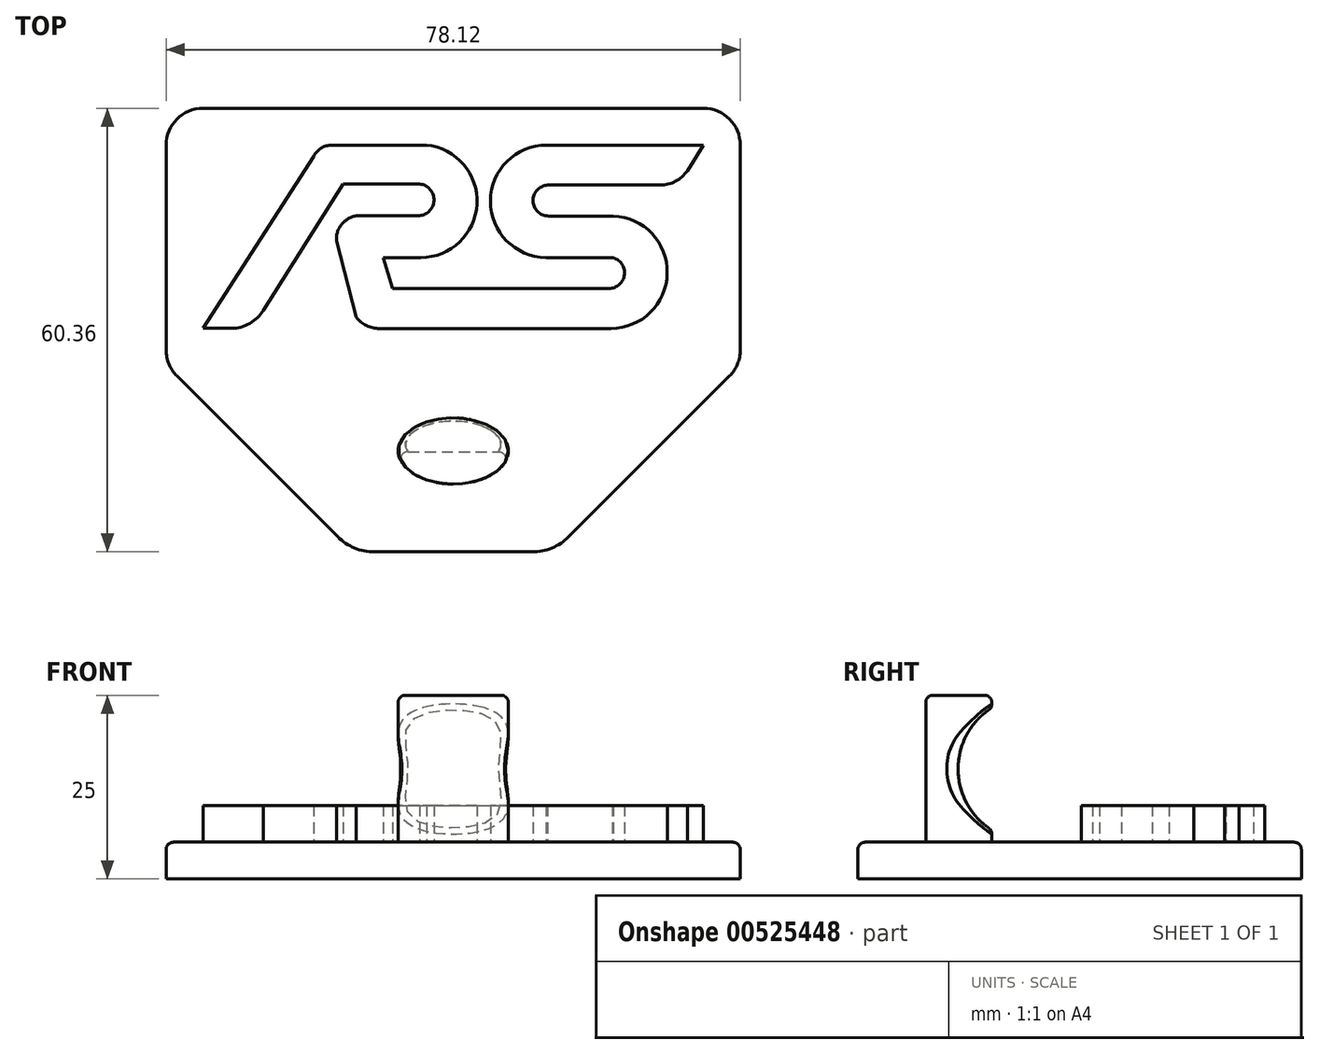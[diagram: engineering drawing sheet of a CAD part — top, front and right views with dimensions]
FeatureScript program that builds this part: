
annotation { "Feature Type Name" : "Feature", "Feature Type Description" : "" }
export const myFeature = defineFeature(function(context is Context, id is Id, definition is map)
    precondition{}
    {
        {
            var Q0;
            Q0=qCreatedBy(makeId("Top.planeOp"),FACE);
            var sketch = newSketch(context, id + "F0", { "sketchPlane" : qUnion([Q0])});
            skLineSegment(sketch, "E0", {"start": v(-38.04, -12.57) * mm, "end": v(-22.97, 10.83) * mm});
            skLineSegment(sketch, "E1", {"start": v(8.97, 2.72) * mm, "end": v(17.8, 2.72) * mm});
            skLineSegment(sketch, "E2", {"start": v(-12.22, -7.15) * mm, "end": v(17.2, -7.15) * mm});
            skLineSegment(sketch, "E3", {"start": v(8.73, 12.37) * mm, "end": v(30.08, 12.37) * mm});
            skLineSegment(sketch, "E4", {"start": v(-18.96, 7.08) * mm, "end": v(-8.76, 7.08) * mm});
            skLineSegment(sketch, "E5", {"start": v(-13.5, -2.94) * mm, "end": v(-8.4, -2.94) * mm});
            skLineSegment(sketch, "E6", {"start": v(8.63, -2.94) * mm, "end": v(17.65, -2.94) * mm});
            skLineSegment(sketch, "E7", {"start": v(-18.96, 7.08) * mm, "end": v(-29.82, -10.1) * mm});
            skLineSegment(sketch, "E8", {"start": v(-38.04, -12.57) * mm, "end": v(-34.18, -12.57) * mm});
            skLineSegment(sketch, "E9", {"start": v(-14.02, -12.59) * mm, "end": v(17.48, -12.59) * mm});
            skLineSegment(sketch, "E10", {"start": v(-8.57, 2.77) * mm, "end": v(-16.7, 2.77) * mm});
            skLineSegment(sketch, "E11", {"start": v(-19.87, -0.65) * mm, "end": v(-17.2, -11.05) * mm});
            skArc(sketch, "E12", {"start": v(-34.18, -12.57) * mm, "mid": v(-31.68, -11.91) * mm, "end": v(-29.82, -10.1) * mm});
            skLineSegment(sketch, "E13", {"start": v(-20.5, 12.37) * mm, "end": v(-7.63, 12.37) * mm});
            skArc(sketch, "E14", {"start": v(-20.5, 12.37) * mm, "mid": v(-21.95, 11.95) * mm, "end": v(-22.97, 10.83) * mm});
            skArc(sketch, "E15", {"start": v(-8.57, 2.77) * mm, "mid": v(-6.6, 5.01) * mm, "end": v(-8.76, 7.08) * mm});
            skArc(sketch, "E16", {"start": v(-16.7, 2.77) * mm, "mid": v(-19.03, 1.75) * mm, "end": v(-19.87, -0.65) * mm});
            skArc(sketch, "E17", {"start": v(-8.4, -2.94) * mm, "mid": v(-0.74, 4.34) * mm, "end": v(-7.63, 12.37) * mm});
            skArc(sketch, "E18", {"start": v(8.73, 12.37) * mm, "mid": v(1.08, 4.76) * mm, "end": v(8.63, -2.94) * mm});
            skArc(sketch, "E19", {"start": v(17.48, -12.59) * mm, "mid": v(25.13, -5.08) * mm, "end": v(17.8, 2.72) * mm});
            skArc(sketch, "E20", {"start": v(17.2, -7.15) * mm, "mid": v(19.32, -5.24) * mm, "end": v(17.65, -2.94) * mm});
            skArc(sketch, "E21", {"start": v(-17.2, -11.05) * mm, "mid": v(-15.78, -12.18) * mm, "end": v(-14.02, -12.59) * mm});
            skLineSegment(sketch, "E22", {"start": v(30.08, 12.37) * mm, "end": v(27.89, 8.87) * mm});
            skLineSegment(sketch, "E23", {"start": v(8.87, 6.92) * mm, "end": v(24.17, 6.92) * mm});
            skArc(sketch, "E24", {"start": v(8.87, 6.92) * mm, "mid": v(6.88, 4.77) * mm, "end": v(8.97, 2.72) * mm});
            skArc(sketch, "E25", {"start": v(24.17, 6.92) * mm, "mid": v(26.27, 7.44) * mm, "end": v(27.89, 8.87) * mm});
            skLineSegment(sketch, "E26", {"start": v(-13.5, -2.94) * mm, "end": v(-12.22, -7.15) * mm});
            skSolve(sketch);
        }
        {
            var Q0;
            Q0 = qSketchRegion(id + "F0", true);
            extrude(context, id + "F1", {"entities" : qUnion([Q0]), "depth" : 5 * mm, "offsetDistance" : 25 * mm});
        }
        {
            var Q0;
            Q0=makeQuery(id+"F1.opExtrude","CAP_FACE",FACE,{"disambiguationData":[OSD([sQuery(id+"F0.wireOp",EDGE,"E0"),sQuery(id+"F0.wireOp",EDGE,"E1"),sQuery(id+"F0.wireOp",EDGE,"E2"),sQuery(id+"F0.wireOp",EDGE,"E3"),sQuery(id+"F0.wireOp",EDGE,"E4"),sQuery(id+"F0.wireOp",EDGE,"E5"),sQuery(id+"F0.wireOp",EDGE,"E6"),sQuery(id+"F0.wireOp",EDGE,"E7"),sQuery(id+"F0.wireOp",EDGE,"E8"),sQuery(id+"F0.wireOp",EDGE,"E9"),sQuery(id+"F0.wireOp",EDGE,"E10"),sQuery(id+"F0.wireOp",EDGE,"E11"),sQuery(id+"F0.wireOp",EDGE,"E12"),sQuery(id+"F0.wireOp",EDGE,"E13"),sQuery(id+"F0.wireOp",EDGE,"E14"),sQuery(id+"F0.wireOp",EDGE,"E15"),sQuery(id+"F0.wireOp",EDGE,"E16"),sQuery(id+"F0.wireOp",EDGE,"E17"),sQuery(id+"F0.wireOp",EDGE,"E18"),sQuery(id+"F0.wireOp",EDGE,"E19"),sQuery(id+"F0.wireOp",EDGE,"E20"),sQuery(id+"F0.wireOp",EDGE,"E21"),sQuery(id+"F0.wireOp",EDGE,"E22"),sQuery(id+"F0.wireOp",EDGE,"E23"),sQuery(id+"F0.wireOp",EDGE,"E24"),sQuery(id+"F0.wireOp",EDGE,"E25"),sQuery(id+"F0.wireOp",EDGE,"E26")])],"isStart":true});
            var sketch = newSketch(context, id + "F2", { "sketchPlane" : qUnion([Q0])});
            skLineSegment(sketch, "E27.bottom", {"start": v(-38.04, -17.37) * mm, "end": v(30.08, -17.37) * mm});
            skLineSegment(sketch, "E27.top", {"start": v(-43.04, 17.59) * mm, "end": v(35.08, 17.59) * mm});
            skLineSegment(sketch, "E27.left", {"start": v(-43.04, -12.37) * mm, "end": v(-43.04, 17.59) * mm});
            skLineSegment(sketch, "E27.right", {"start": v(35.08, -12.37) * mm, "end": v(35.08, 17.59) * mm});
            skPoint(sketch, "E28.visualSharp", {"position": v(-43.04, -17.37) * mm});
            skArc(sketch, "E28.filletArc", {"start": v(-43.04, -12.37) * mm, "mid": v(-41.58, -15.9) * mm, "end": v(-38.04, -17.37) * mm});
            skPoint(sketch, "E29.visualSharp", {"position": v(35.08, -17.37) * mm});
            skArc(sketch, "E29.filletArc", {"start": v(30.08, -17.37) * mm, "mid": v(33.62, -15.9) * mm, "end": v(35.08, -12.37) * mm});
            skPoint(sketch, "E30.visualSharp", {"position": v(-43.04, 17.59) * mm});
            skSolve(sketch);
        }
        {
            var Q0;
            Q0 = qSketchRegion(id + "F2", true);
            extrude(context, id + "F3", {"entities" : qUnion([Q0]), "operationType" : NewBodyOperationType.ADD, "depth" : 5 * mm, "offsetDistance" : 25 * mm});
        }
        {
            var Q0;
            Q0=makeQuery(id+"F3.opExtrude","CAP_FACE",FACE,{"disambiguationData":[OSD([sQuery(id+"F2.wireOp",EDGE,"E27.bottom"),sQuery(id+"F2.wireOp",EDGE,"E27.top"),sQuery(id+"F2.wireOp",EDGE,"E27.left"),sQuery(id+"F2.wireOp",EDGE,"E27.right"),sQuery(id+"F2.wireOp",EDGE,"E28.filletArc"),sQuery(id+"F2.wireOp",EDGE,"E29.filletArc"),sQuery(id+"F2.wireOp",EDGE,"744ff583-1bf7-4c06-8853-35fc34389462.filletArc"),sQuery(id+"F2.wireOp",EDGE,"E30.filletArc")])],"isStart":true});
            var sketch = newSketch(context, id + "F4", { "sketchPlane" : qUnion([Q0])});
            skLineSegment(sketch, "E31", {"start": v(-43.04, -17.59) * mm, "end": v(-19.7, -40.94) * mm});
            skLineSegment(sketch, "E32", {"start": v(35.08, -17.59) * mm, "end": v(11.73, -40.94) * mm});
            skLineSegment(sketch, "E33", {"start": v(-14.74, -42.99) * mm, "end": v(6.78, -42.99) * mm});
            skPoint(sketch, "E34.visualSharp", {"position": v(-17.64, -42.99) * mm});
            skArc(sketch, "E34.filletArc", {"start": v(-19.7, -40.94) * mm, "mid": v(-17.42, -42.45) * mm, "end": v(-14.74, -42.99) * mm});
            skPoint(sketch, "E35.visualSharp", {"position": v(9.68, -42.99) * mm});
            skArc(sketch, "E35.filletArc", {"start": v(6.78, -42.99) * mm, "mid": v(9.46, -42.45) * mm, "end": v(11.73, -40.94) * mm});
            skLineSegment(sketch, "E36", {"start": v(-43.04, -17.59) * mm, "end": v(35.08, -17.59) * mm});
            skSolve(sketch);
        }
        {
            var Q0;
            Q0 = qSketchRegion(id + "F4", true);
            extrude(context, id + "F5", {"entities" : qUnion([Q0]), "operationType" : NewBodyOperationType.ADD, "oppositeDirection" : true, "depth" : 5 * mm, "offsetDistance" : 25 * mm});
        }
        {
            var Q0;
            {var subQ0=sQuery(id+"F2.wireOp",EDGE,"E27.left");Q0=makeQuery(id+"F5.boolean.opBoolean","MERGE",EDGE,{"derivedFrom":[makeQuery(id+"F3.opExtrude","SWEPT_EDGE",EDGE,{"disambiguationData":[OSD([sQuery(id+"F2.wireOp",EDGE,"E27.top"),subQ0])]}),makeQuery(id+"F5.opExtrude","SWEPT_EDGE",EDGE,{"disambiguationData":[OSD([subQ0,sQuery(id+"F4.wireOp",EDGE,"E31"),sQuery(id+"F4.wireOp",EDGE,"E36")])]})]});}
            var Q1;
            {var subQ0=sQuery(id+"F2.wireOp",EDGE,"E27.right");Q1=makeQuery(id+"F5.boolean.opBoolean","MERGE",EDGE,{"derivedFrom":[makeQuery(id+"F3.opExtrude","SWEPT_EDGE",EDGE,{"disambiguationData":[OSD([sQuery(id+"F2.wireOp",EDGE,"E27.top"),subQ0])]}),makeQuery(id+"F5.opExtrude","SWEPT_EDGE",EDGE,{"disambiguationData":[OSD([subQ0,sQuery(id+"F4.wireOp",EDGE,"E32"),sQuery(id+"F4.wireOp",EDGE,"E36")])]})]});}
            fillet(context, id + "F6", {"entities" : qUnion([Q0, Q1]), "radius" : 5 * mm, "tangentPropagation" : true, "allowEdgeOverflow" : false});
        }
        {
            var Q0;
            Q0=makeQuery(id+"F5.boolean.opBoolean","MERGE",FACE,{"derivedFrom":[makeQuery(id+"F3.opExtrude","CAP_FACE",FACE,{"disambiguationData":[OSD([sQuery(id+"F2.wireOp",EDGE,"E27.bottom"),sQuery(id+"F2.wireOp",EDGE,"E27.top"),sQuery(id+"F2.wireOp",EDGE,"E27.left"),sQuery(id+"F2.wireOp",EDGE,"E27.right"),sQuery(id+"F2.wireOp",EDGE,"E28.filletArc"),sQuery(id+"F2.wireOp",EDGE,"E29.filletArc")])],"isStart":true}),makeQuery(id+"F5.opExtrude","CAP_FACE",FACE,{"disambiguationData":[OSD([sQuery(id+"F4.wireOp",EDGE,"E31"),sQuery(id+"F4.wireOp",EDGE,"E32"),sQuery(id+"F4.wireOp",EDGE,"E33"),sQuery(id+"F4.wireOp",EDGE,"E34.filletArc"),sQuery(id+"F4.wireOp",EDGE,"E35.filletArc"),sQuery(id+"F4.wireOp",EDGE,"E36")])],"isStart":true})]});
            var sketch = newSketch(context, id + "F7", { "sketchPlane" : qUnion([Q0])});
            skEllipse(sketch, "E37", {"center": v(-3.98, -29.25) * mm, "majorRadius": 7.5 * mm, "minorRadius": 4.5 * mm, "majorAxis": v(1, 0)});
            skSolve(sketch);
        }
        {
            var Q0;
            Q0 = qSketchRegion(id + "F7", true);
            extrude(context, id + "F8", {"entities" : qUnion([Q0]), "operationType" : NewBodyOperationType.ADD, "depth" : 20 * mm, "offsetDistance" : 25 * mm});
        }
        {
            var Q0;
            Q0=qCreatedBy(makeId("Right.planeOp"),FACE);
            var sketch = newSketch(context, id + "F9", { "sketchPlane" : qUnion([Q0])});
            skArc(sketch, "E38", {"start": v(-9.73, 10.61) * mm, "mid": v(-28.2, 14.58) * mm, "end": v(-14.6, 1.47) * mm});
            skLineSegment(sketch, "E39.bottom", {"start": v(-9.73, 10.61) * mm, "end": v(-14.6, 10.61) * mm});
            skLineSegment(sketch, "E39.right", {"start": v(-14.6, 10.61) * mm, "end": v(-14.6, 1.47) * mm});
            skSolve(sketch);
        }
        {
            var Q0;
            Q0 = qSketchRegion(id + "F9", true);
            extrude(context, id + "F10", {"entities" : qUnion([Q0]), "operationType" : NewBodyOperationType.REMOVE, "endBound" : BoundingType.THROUGH_ALL, "oppositeDirection" : true, "depth" : 25 * mm, "offsetDistance" : 25 * mm});
        }
        {
            var Q0;
            Q0 = qSketchRegion(id + "F9", true);
            extrude(context, id + "F11", {"entities" : qUnion([Q0]), "operationType" : NewBodyOperationType.REMOVE, "depth" : 25 * mm, "offsetDistance" : 25 * mm});
        }
        {
            var Q0;
            Q0=makeQuery(id+"F11.boolean.opBoolean","INTERSECT",EDGE,{"derivedFrom":[makeQuery(id+"F8.opExtrude","SWEPT_FACE",FACE,{"disambiguationData":[OSD([sQuery(id+"F7.wireOp",EDGE,"E37")])]}),makeQuery(id+"F11.opExtrude","SWEPT_FACE",FACE,{"disambiguationData":[OSD([sQuery(id+"F9.wireOp",EDGE,"E38")])]})]});
            var Q1;
            Q1=makeQuery(id+"F8.opExtrude","CAP_EDGE",EDGE,{"disambiguationData":[OSD([sQuery(id+"F7.wireOp",EDGE,"E37")])],"isStart":false});
            var Q2;
            Q2=makeQuery(id+"F5.opExtrude","CAP_EDGE",EDGE,{"disambiguationData":[OSD([sQuery(id+"F4.wireOp",EDGE,"E31")])],"isStart":true});
            fillet(context, id + "F12", {"entities" : qUnion([Q0, Q1, Q2]), "radius" : 1 * mm, "tangentPropagation" : true, "allowEdgeOverflow" : false});
        }
    });
